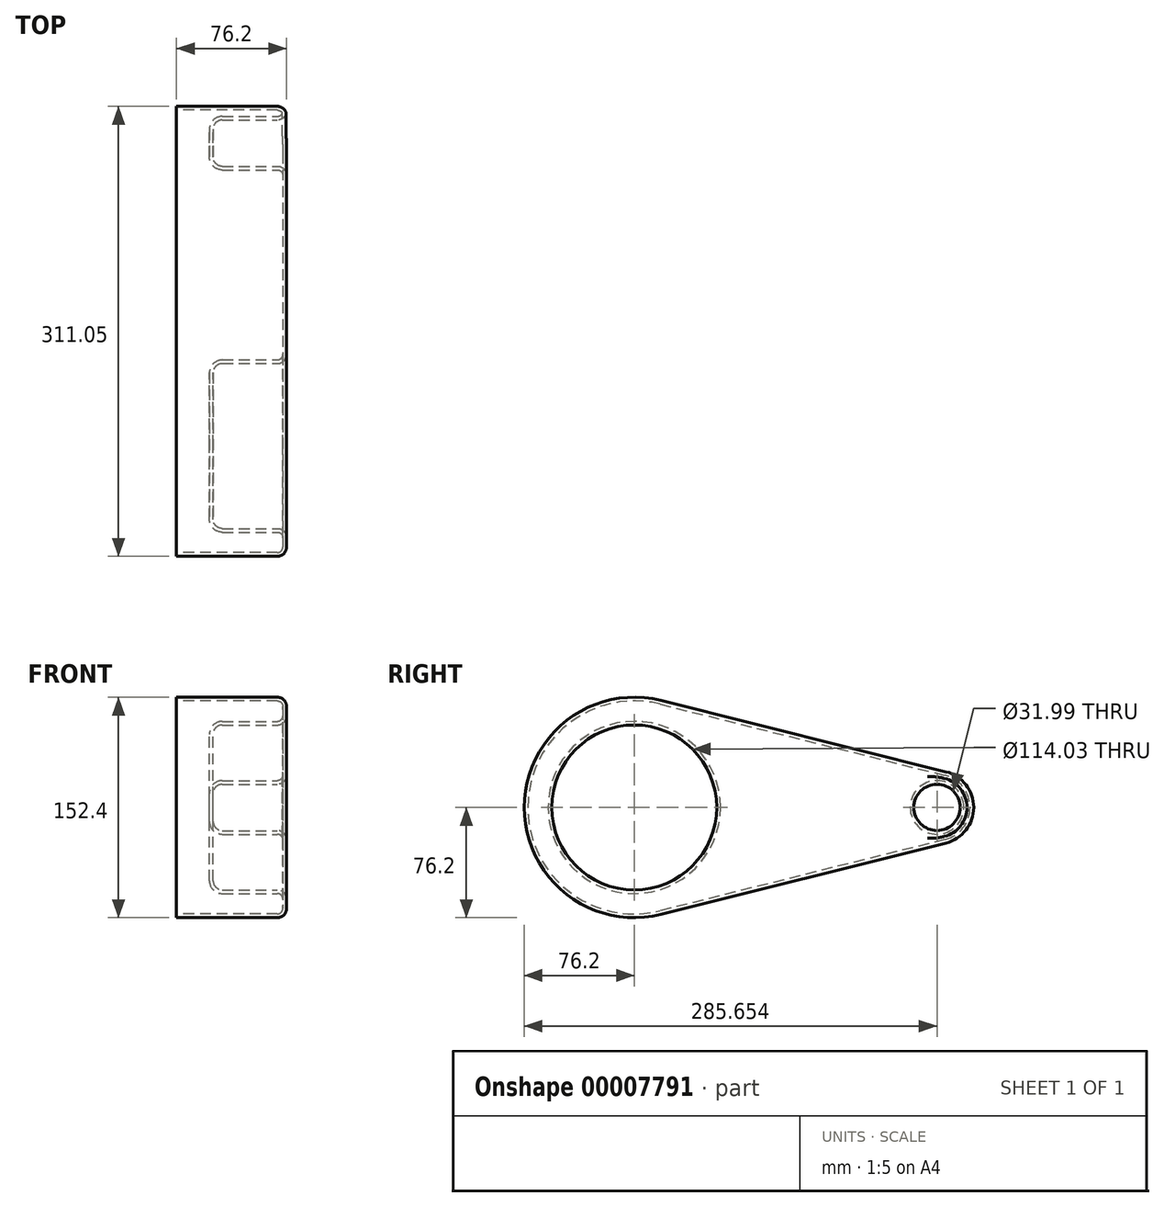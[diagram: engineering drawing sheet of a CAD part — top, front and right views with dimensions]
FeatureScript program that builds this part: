
annotation { "Feature Type Name" : "Feature", "Feature Type Description" : "" }
export const myFeature = defineFeature(function(context is Context, id is Id, definition is map)
    precondition{}
    {
        {
            var Q0;
            Q0=qCreatedBy(makeId("Right.planeOp"),FACE);
            var sketch = newSketch(context, id + "F0", { "sketchPlane" : qUnion([Q0])});
            skCircle(sketch, "E0", {"center": v(0, 0) * mm, "radius": 76.2 * mm});
            skCircle(sketch, "E1", {"center": v(209.45, 0) * mm, "radius": 25.4 * mm});
            skLineSegment(sketch, "E2", {"start": v(18.48, 73.92) * mm, "end": v(215.61, 24.64) * mm});
            skLineSegment(sketch, "E3", {"start": v(215.61, -24.64) * mm, "end": v(18.48, -73.92) * mm});
            skSolve(sketch);
        }
        {
            var Q0;
            {var subQ0=sQuery(id+"F0.wireOp",EDGE,"E1");var subQ2=makeQuery(id+"F0.imprint","INTERSECT",VERTEX,{"derivedFrom":[subQ0,sQuery(id+"F0.wireOp",EDGE,"E2")]});Q0=makeQuery(id+"F0.imprint","IMPRINT",FACE,{"disambiguationData":[TD([[makeQuery(id+"F0.imprint","IMPRINT",EDGE,{"disambiguationData":[TD([[subQ2,-1.0]])],"derivedFrom":subQ0}),1.0]])]});}
            var Q1;
            {var subQ0=sQuery(id+"F0.wireOp",EDGE,"E0");var subQ2=makeQuery(id+"F0.imprint","INTERSECT",VERTEX,{"derivedFrom":[subQ0,sQuery(id+"F0.wireOp",EDGE,"E2")]});Q1=makeQuery(id+"F0.imprint","IMPRINT",FACE,{"disambiguationData":[TD([[makeQuery(id+"F0.imprint","IMPRINT",EDGE,{"disambiguationData":[TD([[subQ2,-1.0]])],"derivedFrom":subQ0}),1.0]])]});}
            var Q2;
            {var subQ1=sQuery(id+"F0.wireOp",EDGE,"E2");Q2=makeQuery(id+"F0.imprint","IMPRINT",FACE,{"disambiguationData":[TD([[makeQuery(id+"F0.imprint","IMPRINT",EDGE,{"derivedFrom":subQ1}),-1.0]])]});}
            extrude(context, id + "F1", {"entities" : qUnion([Q0, Q1, Q2]), "endBound" : BoundingType.SYMMETRIC, "depth" : 76.2 * mm});
        }
        {
            var Q0;
            Q0=makeQuery(id+"F1.opExtrude","CAP_FACE",FACE,{"disambiguationData":[OSD([sQuery(id+"F0.wireOp",EDGE,"E0"),sQuery(id+"F0.wireOp",EDGE,"E1"),sQuery(id+"F0.wireOp",EDGE,"E2"),sQuery(id+"F0.wireOp",EDGE,"E3")])],"isStart":false});
            var sketch = newSketch(context, id + "F2", { "sketchPlane" : qUnion([Q0])});
            skCircle(sketch, "E4", {"center": v(0, 0) * mm, "radius": 57.02 * mm});
            skCircle(sketch, "E5", {"center": v(209.45, 0) * mm, "radius": 16 * mm});
            skSolve(sketch);
        }
        {
            var Q0;
            Q0=makeQuery(id+"F2.imprint","IMPRINT",FACE,{"disambiguationData":[TD([[makeQuery(id+"F2.imprint","IMPRINT",EDGE,{"derivedFrom":sQuery(id+"F2.wireOp",EDGE,"E4")}),1.0]])]});
            var Q1;
            Q1=makeQuery(id+"F2.imprint","IMPRINT",FACE,{"disambiguationData":[TD([[makeQuery(id+"F2.imprint","IMPRINT",EDGE,{"derivedFrom":sQuery(id+"F2.wireOp",EDGE,"E5")}),1.0]])]});
            extrude(context, id + "F3", {"entities" : qUnion([Q0, Q1]), "operationType" : NewBodyOperationType.REMOVE, "oppositeDirection" : true, "depth" : 50.8 * mm});
        }
        {
            var Q0;
            Q0=makeQuery(id+"F1.opExtrude","CAP_FACE",FACE,{"disambiguationData":[OSD([sQuery(id+"F0.wireOp",EDGE,"E0"),sQuery(id+"F0.wireOp",EDGE,"E1"),sQuery(id+"F0.wireOp",EDGE,"E2"),sQuery(id+"F0.wireOp",EDGE,"E3")])],"isStart":false});
            var Q1;
            Q1=makeQuery(id+"F3.boolean.opBoolean","COPY",FACE,{"derivedFrom":makeQuery(id+"F3.opExtrude","CAP_FACE",FACE,{"disambiguationData":[OSD([sQuery(id+"F2.wireOp",EDGE,"E4")])],"isStart":false})});
            var Q2;
            Q2=makeQuery(id+"F3.boolean.opBoolean","COPY",FACE,{"derivedFrom":makeQuery(id+"F3.opExtrude","CAP_FACE",FACE,{"disambiguationData":[OSD([sQuery(id+"F2.wireOp",EDGE,"E5")])],"isStart":false})});
            fillet(context, id + "F4", {"entities" : qUnion([Q0, Q1, Q2]), "radius" : 6.35 * mm, "tangentPropagation" : true, "allowEdgeOverflow" : false});
        }
        {
            var Q0;
            Q0=makeQuery(id+"F1.opExtrude","CAP_FACE",FACE,{"disambiguationData":[OSD([sQuery(id+"F0.wireOp",EDGE,"E0"),sQuery(id+"F0.wireOp",EDGE,"E1"),sQuery(id+"F0.wireOp",EDGE,"E2"),sQuery(id+"F0.wireOp",EDGE,"E3")])],"isStart":true});
            shell(context, id + "F5", {"entities" : qUnion([Q0]), "thickness" : 2.54 * mm});
        }
    });
